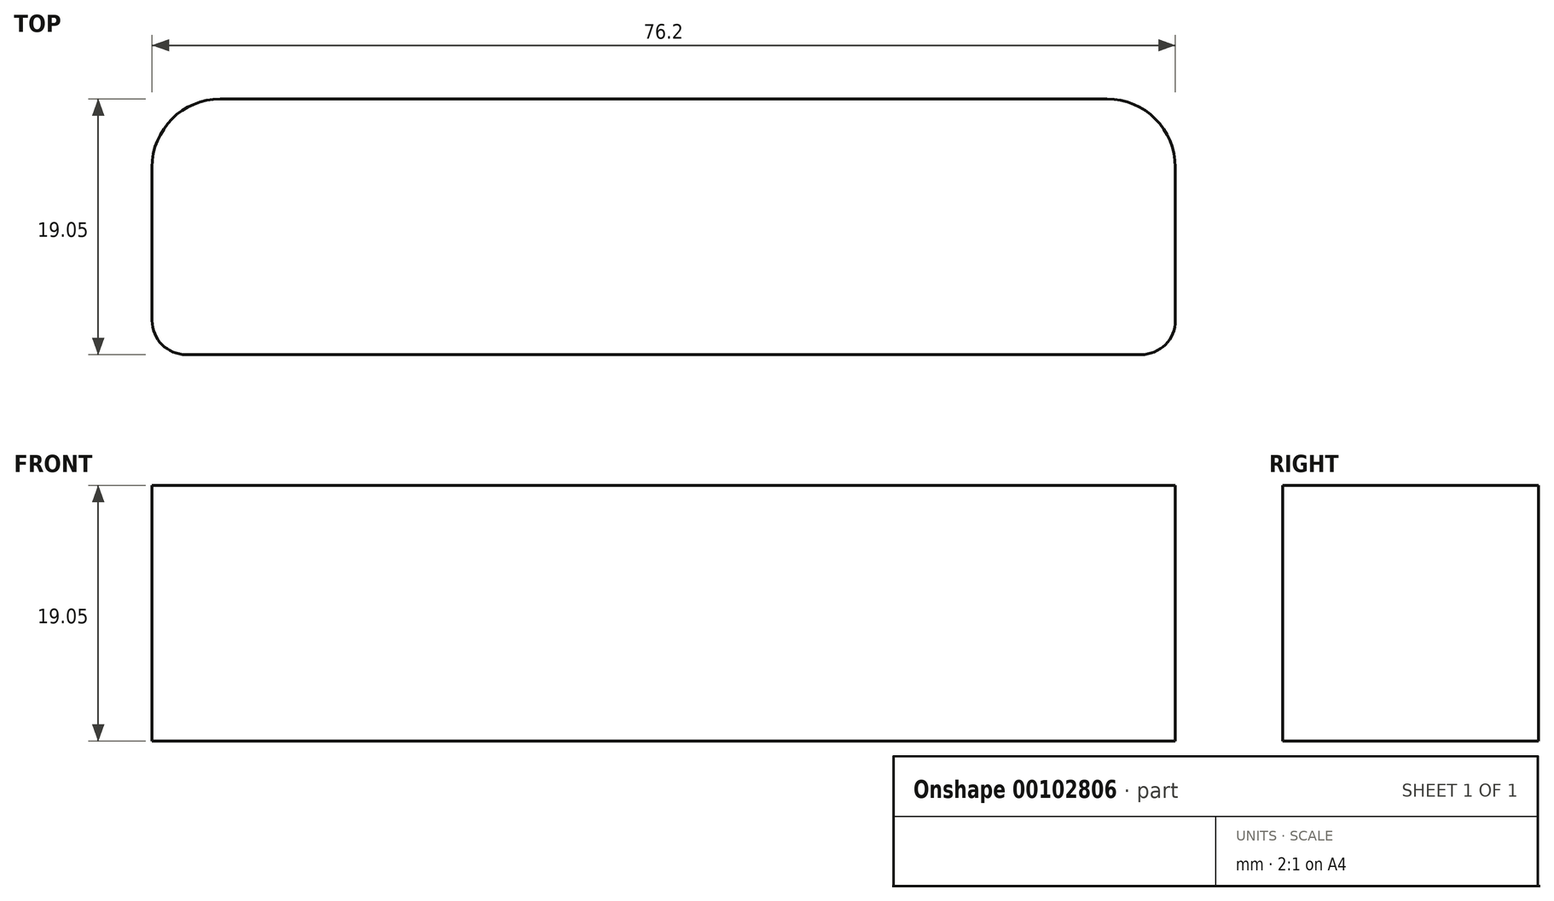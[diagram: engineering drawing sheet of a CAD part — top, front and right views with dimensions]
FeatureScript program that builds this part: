
annotation { "Feature Type Name" : "Feature", "Feature Type Description" : "" }
export const myFeature = defineFeature(function(context is Context, id is Id, definition is map)
    precondition{}
    {
        {
            var Q0;
            Q0=qCreatedBy(makeId("Top.planeOp"),FACE);
            var sketch = newSketch(context, id + "F0", { "sketchPlane" : qUnion([Q0])});
            skLineSegment(sketch, "E0.bottom", {"start": v(2.54, 0) * mm, "end": v(73.66, 0) * mm});
            skLineSegment(sketch, "E0.top", {"start": v(5.08, 19.05) * mm, "end": v(71.12, 19.05) * mm});
            skLineSegment(sketch, "E0.left", {"start": v(0, 2.54) * mm, "end": v(0, 13.97) * mm});
            skLineSegment(sketch, "E0.right", {"start": v(76.2, 2.54) * mm, "end": v(76.2, 13.97) * mm});
            skPoint(sketch, "E1.visualSharp", {"position": v(0, 19.05) * mm});
            skArc(sketch, "E1.filletArc", {"start": v(5.08, 19.05) * mm, "mid": v(1.49, 17.56) * mm, "end": v(0, 13.97) * mm});
            skPoint(sketch, "E2.visualSharp", {"position": v(76.2, 19.05) * mm});
            skArc(sketch, "E2.filletArc", {"start": v(76.2, 13.97) * mm, "mid": v(74.71, 17.56) * mm, "end": v(71.12, 19.05) * mm});
            skPoint(sketch, "E3.visualSharp", {"position": v(0, 0) * mm});
            skArc(sketch, "E3.filletArc", {"start": v(0, 2.54) * mm, "mid": v(0.74, 0.74) * mm, "end": v(2.54, 0) * mm});
            skPoint(sketch, "E4.visualSharp", {"position": v(76.2, 0) * mm});
            skArc(sketch, "E4.filletArc", {"start": v(73.66, 0) * mm, "mid": v(75.46, 0.74) * mm, "end": v(76.2, 2.54) * mm});
            skSolve(sketch);
        }
        {
            var Q0;
            Q0=makeQuery(id+"F0.imprint","IMPRINT",FACE,{"disambiguationData":[TD([[makeQuery(id+"F0.imprint","IMPRINT",EDGE,{"derivedFrom":sQuery(id+"F0.wireOp",EDGE,"E0.bottom")}),1.0]])]});
            extrude(context, id + "F1", {"entities" : qUnion([Q0]), "depth" : 19.05 * mm});
        }
    });
